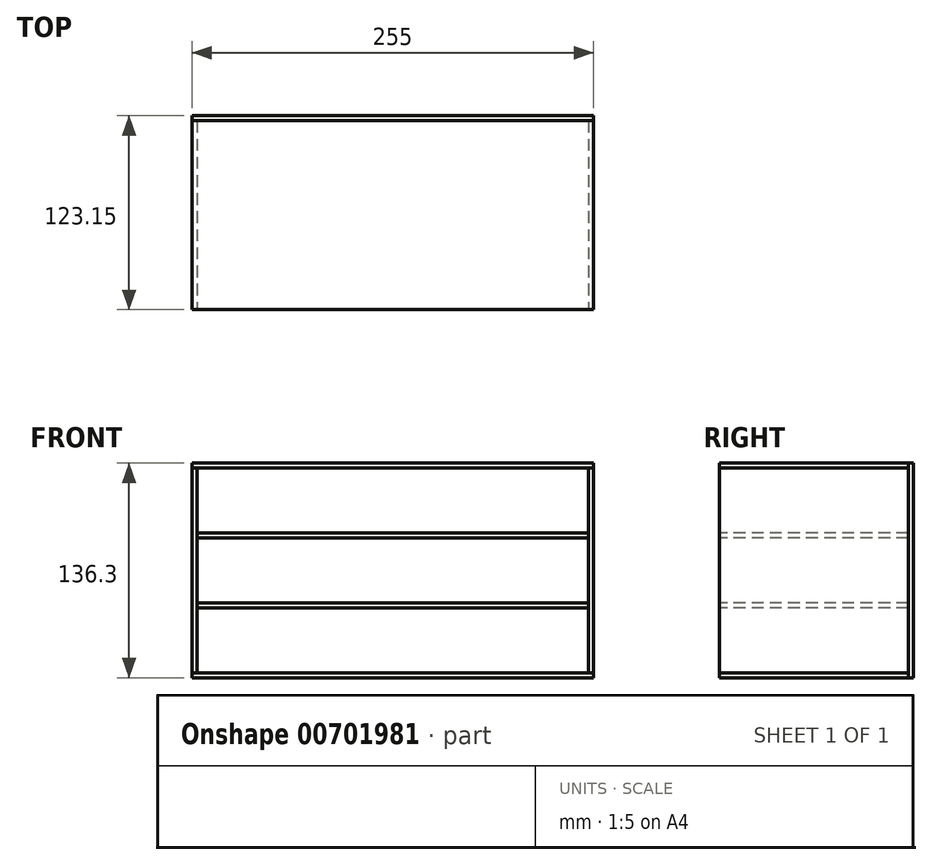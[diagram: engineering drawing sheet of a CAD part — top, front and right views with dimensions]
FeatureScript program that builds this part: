
annotation { "Feature Type Name" : "Feature", "Feature Type Description" : "" }
export const myFeature = defineFeature(function(context is Context, id is Id, definition is map)
    precondition{}
    {
        {
            assignVariable(context, id + "F0", {"name" : "x", "anyValue" : 3.15});
        }
        {
            var Q0;
            Q0=qCreatedBy(makeId("Top.planeOp"),FACE);
            var sketch = newSketch(context, id + "F1", { "sketchPlane" : qUnion([Q0])});
            skLineSegment(sketch, "E0.bottom", {"start": v(0, 0) * mm, "end": v(255, 0) * mm});
            skLineSegment(sketch, "E0.top", {"start": v(0, 120) * mm, "end": v(255, 120) * mm});
            skLineSegment(sketch, "E0.left", {"start": v(0, 0) * mm, "end": v(0, 120) * mm});
            skLineSegment(sketch, "E0.right", {"start": v(255, 0) * mm, "end": v(255, 120) * mm});
            skSolve(sketch);
        }
        {
            var Q0;
            Q0=qSketchRegion(id+"F1",true);
            extrude(context, id + "F2", {"entities" : qUnion([Q0]), "depth" : (getVariable(context, 'x')) * mm, "offsetDistance" : 25 * mm});
        }
        {
            var Q0;
            Q0=makeQuery(id+"F2.opExtrude","SWEPT_FACE",FACE,{"disambiguationData":[OSD([sQuery(id+"F1.wireOp",EDGE,"E0.left")])]});
            var sketch = newSketch(context, id + "F3", { "sketchPlane" : qUnion([Q0])});
            skLineSegment(sketch, "E1.top", {"start": v(0, 133.15) * mm, "end": v(-120, 133.15) * mm});
            skLineSegment(sketch, "E1.left", {"start": v(0, 3.15) * mm, "end": v(0, 133.15) * mm});
            skLineSegment(sketch, "E2", {"start": v(0, 3.15) * mm, "end": v(-120, 3.15) * mm});
            skLineSegment(sketch, "E3", {"start": v(-120, 3.15) * mm, "end": v(-120, 133.15) * mm});
            skSolve(sketch);
        }
        {
            var Q0;
            Q0=qSketchRegion(id+"F3",true);
            extrude(context, id + "F4", {"entities" : qUnion([Q0]), "oppositeDirection" : true, "depth" : (getVariable(context, 'x')) * mm, "offsetDistance" : 25 * mm});
        }
        {
            var Q0;
            Q0=makeQuery(id+"FVTuVMvbx6C6lcW_2.boolean.opBoolean","MERGE",FACE,{"derivedFrom":[makeQuery(id+"F4.opExtrude","SWEPT_FACE",FACE,{"disambiguationData":[OSD([sQuery(id+"F3.wireOp",EDGE,"E1.left")])]}),makeQuery(id+"FVTuVMvbx6C6lcW_2.opExtrude","SWEPT_FACE",FACE,{"disambiguationData":[OSD([sQuery(id+"F9WBSx8lvzqTq6O_2.wireOp",EDGE,"DdJYWYcg-8VXy-0sGO-iMAo-MInbchsGbsPU")])]})]});
            var sketch = newSketch(context, id + "F5", { "sketchPlane" : qUnion([Q0])});
            skLineSegment(sketch, "E4.bottom", {"start": v(3.15, 47.53) * mm, "end": v(251.85, 47.53) * mm});
            skLineSegment(sketch, "E4.top", {"start": v(3.15, 44.38) * mm, "end": v(251.85, 44.38) * mm});
            skLineSegment(sketch, "E4.right", {"start": v(251.85, 47.53) * mm, "end": v(251.85, 44.38) * mm});
            skLineSegment(sketch, "E5", {"start": v(251.85, 3.15) * mm, "end": v(251.85, 44.38) * mm, "construction": true});
            skLineSegment(sketch, "E6", {"start": v(3.15, 44.38) * mm, "end": v(3.15, 47.53) * mm});
            skLineSegment(sketch, "E7.bottom", {"start": v(3.15, 91.92) * mm, "end": v(251.85, 91.92) * mm});
            skLineSegment(sketch, "E7.top", {"start": v(3.15, 88.77) * mm, "end": v(251.85, 88.77) * mm});
            skLineSegment(sketch, "E7.right", {"start": v(251.85, 91.92) * mm, "end": v(251.85, 88.77) * mm});
            skLineSegment(sketch, "E8", {"start": v(3.15, 88.77) * mm, "end": v(3.15, 91.92) * mm});
            skLineSegment(sketch, "E9", {"start": v(251.85, 47.53) * mm, "end": v(251.85, 88.77) * mm, "construction": true});
            skLineSegment(sketch, "E10", {"start": v(251.85, 91.92) * mm, "end": v(251.85, 133.15) * mm, "construction": true});
            skSolve(sketch);
        }
        {
            var Q0;
            Q0=qSketchRegion(id+"F5",true);
            var Q1;
            Q1=makeQuery(id+"F4.opExtrude","SWEPT_FACE",FACE,{"disambiguationData":[OSD([sQuery(id+"F3.wireOp",EDGE,"E3")])]});
            extrude(context, id + "F6", {"entities" : qUnion([Q0]), "endBound" : BoundingType.UP_TO_SURFACE, "oppositeDirection" : true, "depth" : 25 * mm, "endBoundEntityFace" : qUnion([Q1]), "offsetDistance" : 25 * mm});
        }
        {
            var Q0;
            Q0=makeQuery(id+"F2.opExtrude","SWEPT_BODY",BODY,{"disambiguationData":[OSD([sQuery(id+"F1.wireOp",EDGE,"E0.bottom"),sQuery(id+"F1.wireOp",EDGE,"E0.top"),sQuery(id+"F1.wireOp",EDGE,"E0.left"),sQuery(id+"F1.wireOp",EDGE,"E0.right")])]});
            transform(context, id + "F7", {"entities" : qUnion([Q0]), "transformType" : TransformType.TRANSLATION_3D, "dx" : 0 * mm, "dy" : 0 * mm, "dz" : 133.15 * mm, "makeCopy" : true});
        }
        {
            var Q0;
            Q0=makeQuery(id+"F4.opExtrude","SWEPT_BODY",BODY,{"disambiguationData":[OSD([sQuery(id+"F3.wireOp",EDGE,"E1.top"),sQuery(id+"F3.wireOp",EDGE,"E1.left"),sQuery(id+"F3.wireOp",EDGE,"E2"),sQuery(id+"F3.wireOp",EDGE,"E3")])]});
            transform(context, id + "F8", {"entities" : qUnion([Q0]), "transformType" : TransformType.TRANSLATION_3D, "dx" : (263.7 + 3.15 - 15) * mm, "dy" : 0 * mm, "dz" : 0 * mm, "makeCopy" : true});
        }
        {
            var Q0;
            Q0=makeQuery(id+"F7.opPattern","COPY",FACE,{"derivedFrom":makeQuery(id+"F2.opExtrude","SWEPT_FACE",FACE,{"disambiguationData":[OSD([sQuery(id+"F1.wireOp",EDGE,"E0.top")])]}),"instanceName":"1"});
            var sketch = newSketch(context, id + "F9", { "sketchPlane" : qUnion([Q0])});
            skLineSegment(sketch, "E11.bottom", {"start": v(-255, 136.3) * mm, "end": v(0, 136.3) * mm});
            skLineSegment(sketch, "E11.top", {"start": v(-255, 0) * mm, "end": v(0, 0) * mm});
            skLineSegment(sketch, "E11.left", {"start": v(-255, 136.3) * mm, "end": v(-255, 0) * mm});
            skLineSegment(sketch, "E11.right", {"start": v(0, 136.3) * mm, "end": v(0, 0) * mm});
            skSolve(sketch);
        }
        {
            var Q0;
            Q0=qSketchRegion(id+"F9",true);
            extrude(context, id + "F10", {"entities" : qUnion([Q0]), "depth" : (getVariable(context, 'x')) * mm, "offsetDistance" : 25 * mm});
        }
    });
